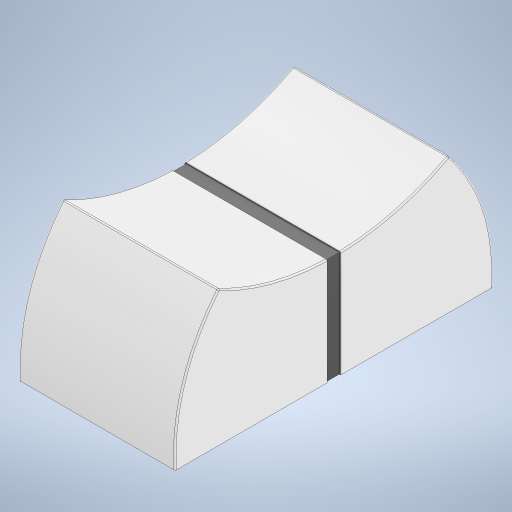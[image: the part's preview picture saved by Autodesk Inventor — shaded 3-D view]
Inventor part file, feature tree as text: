
AUTODESK INVENTOR PART (.ipt)
format: ipt  version: 2023 (Build 270158000, 158)  size: 282,624 bytes
history: native  units: in
note: dims shown in document units (in); Inventor stores cm internally (conversion verified against a paired STEP export)
features: sketch x5, extrude x4, mirror x1, plane x1, fillet x1
ambient origin geometry x8: Origin, YZ Plane, XZ Plane, XY Plane, X Axis, Y Axis, Z Axis, Center Point
bodies: Solid1 (feature_tree)
feature tree (12):
  sketch  "Sketch2"  dims[d0=0.9252in d1=0.3937in d2=0.9252in]
  extrude  "Extrusion1"  Depth=0.3937in
  extrude  "Extrusion2"  Depth=0.6693in
  extrude  "Extrusion3"  Depth=0.4528in TaperAngle=0.0deg
  mirror  "Mirror1"
  plane  "Work Plane1"
  extrude  "Extrusion4"  Depth=0.1575in
  fillet  "Fillet1"  Radius=0.2362in
  sketch  "Sketch3"  dims[d3=0.0394in d4=0.6693in]
  sketch  "Sketch4"  dims[d5=0.7087in d6=0.4528in d7=0.0in]
  sketch  "Sketch5"  dims[d8=0.0787in d9=0.1575in d10=0.2362in d11=0.0in]
  sketch  "Sketch6"  dims[d12=0.0394in d13=0.0039in d14=0.0in d15=0.0866in d16=0.0in d17=0.0039in]
